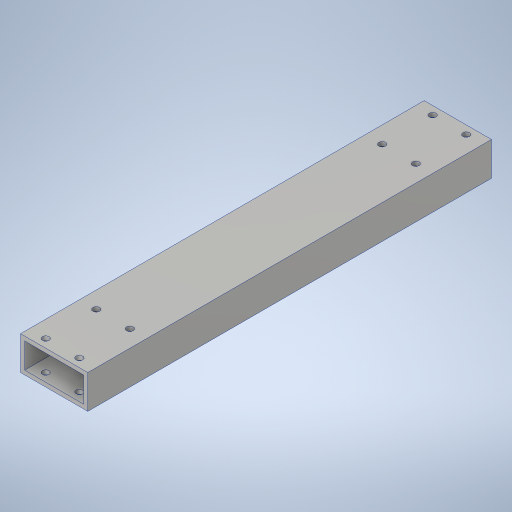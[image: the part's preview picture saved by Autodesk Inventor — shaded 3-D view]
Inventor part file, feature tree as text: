
AUTODESK INVENTOR PART (.ipt)
format: ipt  version: 2023.4 (Build 274418000, 418)  size: 259,072 bytes
history: native  units: in
note: dims shown in document units (in); Inventor stores cm internally (conversion verified against a paired STEP export)
features: sketch x2, extrude x1, hole x1
ambient origin geometry x8: Origin, YZ Plane, XZ Plane, XY Plane, X Axis, Y Axis, Z Axis, Center Point
bodies: Solid1 (feature_tree)
feature tree (4):
  extrude  "Extrusion1"  Depth=1.0in
  hole  "Hole1"  [1 undecoded]
  sketch  "Sketch1"  dims[d0=2.0in d1=1.0in]
  sketch  "Sketch2"  dims[d2=0.125in d3=0.125in d4=12.0in d5=0.0in d6=0.25in d7=1.0in d8=1.5in d9=0.25in d10=0.5in d11=0.5in d12=0.5in d13=1.5in d14=0.201in d15=0.75in d16=0.375in d17=0.25in d18=0.5635in d19=1.0in d20=0.8108in]
note: 1 required parameter value undecoded (feature->parameter linkage not recoverable at this tier; creation-order binding heuristic only, values carry confidence <= 0.55)
